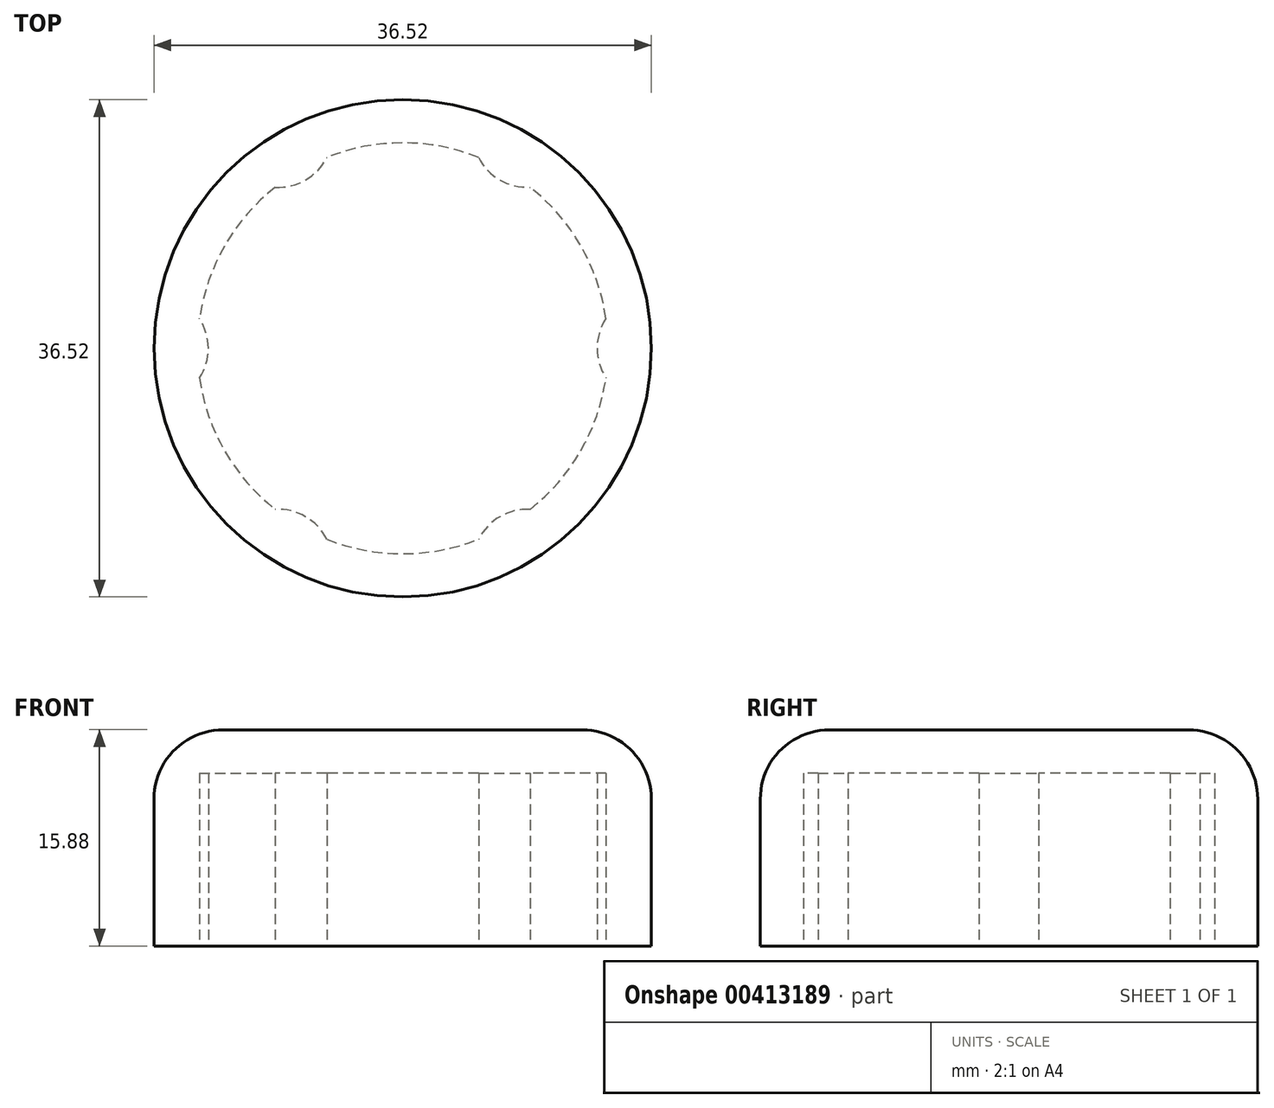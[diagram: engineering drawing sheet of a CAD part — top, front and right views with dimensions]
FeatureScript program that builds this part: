
annotation { "Feature Type Name" : "Feature", "Feature Type Description" : "" }
export const myFeature = defineFeature(function(context is Context, id is Id, definition is map)
    precondition{}
    {
        {
            var Q0;
            Q0=qCreatedBy(makeId("Top.planeOp"),FACE);
            var sketch = newSketch(context, id + "F0", { "sketchPlane" : qUnion([Q0])});
            skCircle(sketch, "E0", {"center": v(0, 0) * mm, "radius": 14.33 * mm});
            skSolve(sketch);
        }
        {
            var Q0;
            Q0=qCreatedBy(makeId("Top.planeOp"),FACE);
            var sketch = newSketch(context, id + "F1", { "sketchPlane" : qUnion([Q0])});
            skCircle(sketch, "E1", {"center": v(0, 0) * mm, "radius": 15.09 * mm});
            skCircle(sketch, "E2.0", {"center": v(0, 0) * mm, "radius": 18.26 * mm});
            skSolve(sketch);
        }
        {
            var Q0;
            Q0=qSketchRegion(id+"F1",true);
            extrude(context, id + "F2", {"entities" : qUnion([Q0]), "depth" : 12.7 * mm});
        }
        {
            var Q0;
            Q0=makeQuery(id+"F2.opExtrude","CAP_FACE",FACE,{"disambiguationData":[OSD([sQuery(id+"F1.wireOp",EDGE,"E1"),sQuery(id+"F1.wireOp",EDGE,"E2.0")])],"isStart":false});
            var sketch = newSketch(context, id + "F3", { "sketchPlane" : qUnion([Q0])});
            skCircle(sketch, "E3", {"center": v(0, 0) * mm, "radius": 18.26 * mm});
            skSolve(sketch);
        }
        {
            var Q0;
            Q0=qSketchRegion(id+"F3",true);
            extrude(context, id + "F4", {"entities" : qUnion([Q0]), "operationType" : NewBodyOperationType.ADD, "depth" : 3.17 * mm});
        }
        {
            var Q0;
            Q0=makeQuery(id+"F2.opExtrude","CAP_FACE",FACE,{"disambiguationData":[OSD([sQuery(id+"F1.wireOp",EDGE,"E1"),sQuery(id+"F1.wireOp",EDGE,"E2.0")])],"isStart":true});
            var sketch = newSketch(context, id + "F5", { "sketchPlane" : qUnion([Q0])});
            skArc(sketch, "E4", {"start": v(-17.83, -3.96) * mm, "mid": v(-14.27, 0) * mm, "end": v(-17.83, 3.96) * mm});
            skLineSegment(sketch, "E5", {"start": v(-14.27, 0) * mm, "end": v(-14.33, 0) * mm, "construction": true});
            skArc(sketch, "E6", {"start": v(-17.83, 3.96) * mm, "mid": v(-18.26, 0) * mm, "end": v(-17.83, -3.96) * mm});
            skArc(sketch, "E7.1.0", {"start": v(-5.48, -17.42) * mm, "mid": v(-7.14, -12.36) * mm, "end": v(-12.35, -13.46) * mm});
            skArc(sketch, "E7.1.1", {"start": v(-12.35, -13.46) * mm, "mid": v(-9.13, -15.82) * mm, "end": v(-5.48, -17.42) * mm});
            skArc(sketch, "E7.2.0", {"start": v(12.35, -13.46) * mm, "mid": v(7.14, -12.36) * mm, "end": v(5.48, -17.42) * mm});
            skArc(sketch, "E7.2.1", {"start": v(5.48, -17.42) * mm, "mid": v(9.13, -15.82) * mm, "end": v(12.35, -13.46) * mm});
            skArc(sketch, "E7.3.0", {"start": v(17.83, 3.96) * mm, "mid": v(14.27, 0) * mm, "end": v(17.83, -3.96) * mm});
            skArc(sketch, "E7.3.1", {"start": v(17.83, -3.96) * mm, "mid": v(18.26, 0) * mm, "end": v(17.83, 3.96) * mm});
            skArc(sketch, "E7.4.0", {"start": v(5.48, 17.42) * mm, "mid": v(7.14, 12.36) * mm, "end": v(12.35, 13.46) * mm});
            skArc(sketch, "E7.4.1", {"start": v(12.35, 13.46) * mm, "mid": v(9.13, 15.82) * mm, "end": v(5.48, 17.42) * mm});
            skArc(sketch, "E7.5.0", {"start": v(-12.35, 13.46) * mm, "mid": v(-7.14, 12.36) * mm, "end": v(-5.48, 17.42) * mm});
            skArc(sketch, "E7.5.1", {"start": v(-5.48, 17.42) * mm, "mid": v(-9.13, 15.82) * mm, "end": v(-12.35, 13.46) * mm});
            skSolve(sketch);
        }
        {
            var Q0;
            Q0 = qSketchRegion(id + "F5", true);
            var Q1;
            Q1=makeQuery(id+"F4.opExtrude","CAP_FACE",FACE,{"disambiguationData":[OSD([sQuery(id+"F3.wireOp",EDGE,"E3")])],"isStart":true});
            extrude(context, id + "F6", {"entities" : qUnion([Q0]), "operationType" : NewBodyOperationType.ADD, "endBound" : BoundingType.UP_TO_SURFACE, "oppositeDirection" : true, "endBoundEntityFace" : qUnion([Q1]), "depth" : 25.4 * mm});
        }
        {
            var Q0;
            Q0=makeQuery(id+"F4.opExtrude","CAP_EDGE",EDGE,{"disambiguationData":[OSD([sQuery(id+"F3.wireOp",EDGE,"E3")])],"isStart":false});
            fillet(context, id + "F7", {"entities" : qUnion([Q0]), "radius" : 5.08 * mm, "tangentPropagation" : true, "allowEdgeOverflow" : false});
        }
    });
